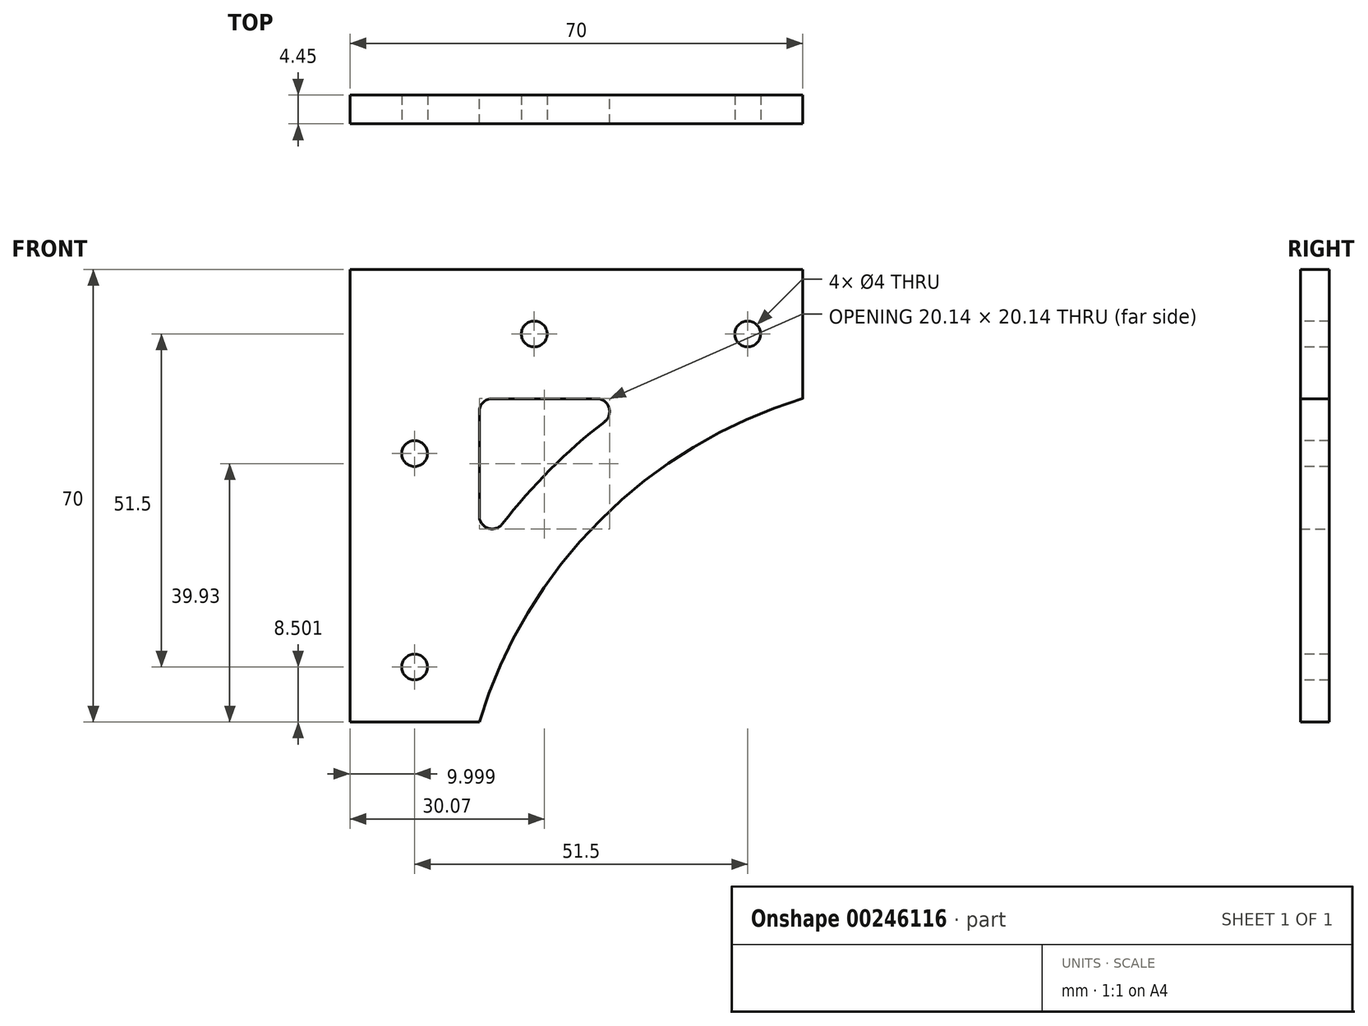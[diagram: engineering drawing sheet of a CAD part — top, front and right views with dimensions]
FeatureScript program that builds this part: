
annotation { "Feature Type Name" : "Feature", "Feature Type Description" : "" }
export const myFeature = defineFeature(function(context is Context, id is Id, definition is map)
    precondition{}
    {
        {
            var Q0;
            Q0=qCreatedBy(makeId("Front.planeOp"),FACE);
            var sketch = newSketch(context, id + "F0", { "sketchPlane" : qUnion([Q0])});
            skLineSegment(sketch, "E0", {"start": v(-71.77, 21.77) * mm, "end": v(-91.77, 21.77) * mm});
            skLineSegment(sketch, "E1", {"start": v(-91.77, 21.77) * mm, "end": v(-91.77, 91.77) * mm});
            skLineSegment(sketch, "E2", {"start": v(-91.77, 91.77) * mm, "end": v(-21.77, 91.77) * mm});
            skLineSegment(sketch, "E3", {"start": v(-21.77, 91.77) * mm, "end": v(-21.77, 71.77) * mm});
            skArc(sketch, "E4", {"start": v(-71.77, 21.77) * mm, "mid": v(-53.03, 53.03) * mm, "end": v(-21.77, 71.77) * mm});
            skArc(sketch, "E5.0", {"start": v(-68.19, 52.4) * mm, "mid": v(-60.81, 60.81) * mm, "end": v(-52.4, 68.19) * mm});
            skLineSegment(sketch, "E6", {"start": v(-53.63, 71.77) * mm, "end": v(-69.77, 71.77) * mm});
            skLineSegment(sketch, "E7", {"start": v(-71.77, 69.77) * mm, "end": v(-71.77, 53.63) * mm});
            skPoint(sketch, "E8.visualSharp", {"position": v(-71.77, 71.77) * mm});
            skArc(sketch, "E8.filletArc", {"start": v(-69.77, 71.77) * mm, "mid": v(-71.18, 71.18) * mm, "end": v(-71.77, 69.77) * mm});
            skPoint(sketch, "E9.visualSharp", {"position": v(-47.38, 71.77) * mm});
            skArc(sketch, "E9.filletArc", {"start": v(-52.4, 68.19) * mm, "mid": v(-51.74, 70.41) * mm, "end": v(-53.63, 71.77) * mm});
            skPoint(sketch, "E10.visualSharp", {"position": v(-71.77, 47.38) * mm});
            skArc(sketch, "E10.filletArc", {"start": v(-71.77, 53.63) * mm, "mid": v(-70.41, 51.74) * mm, "end": v(-68.19, 52.4) * mm});
            skSolve(sketch);
        }
        {
            var Q0;
            Q0=makeQuery(id+"F0.imprint","IMPRINT",FACE,{"disambiguationData":[TD([[makeQuery(id+"F0.imprint","IMPRINT",EDGE,{"derivedFrom":sQuery(id+"F0.wireOp",EDGE,"E0")}),-1.0]])]});
            extrude(context, id + "F1", {"entities" : qUnion([Q0]), "depth" : 4.44 * mm});
        }
        {
            var Q0;
            Q0=makeQuery(id+"F1.opExtrude","CAP_FACE",FACE,{"disambiguationData":[OSD([sQuery(id+"F0.wireOp",EDGE,"E0"),sQuery(id+"F0.wireOp",EDGE,"E1"),sQuery(id+"F0.wireOp",EDGE,"E2"),sQuery(id+"F0.wireOp",EDGE,"E3"),sQuery(id+"F0.wireOp",EDGE,"E4"),sQuery(id+"F0.wireOp",EDGE,"E5.0"),sQuery(id+"F0.wireOp",EDGE,"E6"),sQuery(id+"F0.wireOp",EDGE,"E7"),sQuery(id+"F0.wireOp",EDGE,"E8.filletArc"),sQuery(id+"F0.wireOp",EDGE,"E9.filletArc"),sQuery(id+"F0.wireOp",EDGE,"E10.filletArc")])],"isStart":false});
            var sketch = newSketch(context, id + "F2", { "sketchPlane" : qUnion([Q0])});
            skCircle(sketch, "E11", {"center": v(-63.27, 81.77) * mm, "radius": 2 * mm});
            skCircle(sketch, "E12", {"center": v(-30.27, 81.77) * mm, "radius": 2 * mm});
            skLineSegment(sketch, "E13", {"start": v(-91.77, 91.77) * mm, "end": v(0, 0) * mm, "construction": true});
            skCircle(sketch, "E14.MirrorC", {"center": v(-81.77, 63.27) * mm, "radius": 2 * mm});
            skCircle(sketch, "E15.MirrorC", {"center": v(-81.77, 30.27) * mm, "radius": 2 * mm});
            skSolve(sketch);
        }
        {
            var Q0;
            Q0 = qSketchRegion(id + "F2", true);
            extrude(context, id + "F3", {"entities" : qUnion([Q0]), "operationType" : NewBodyOperationType.REMOVE, "endBound" : BoundingType.THROUGH_ALL, "oppositeDirection" : true, "depth" : 25 * mm});
        }
    });
